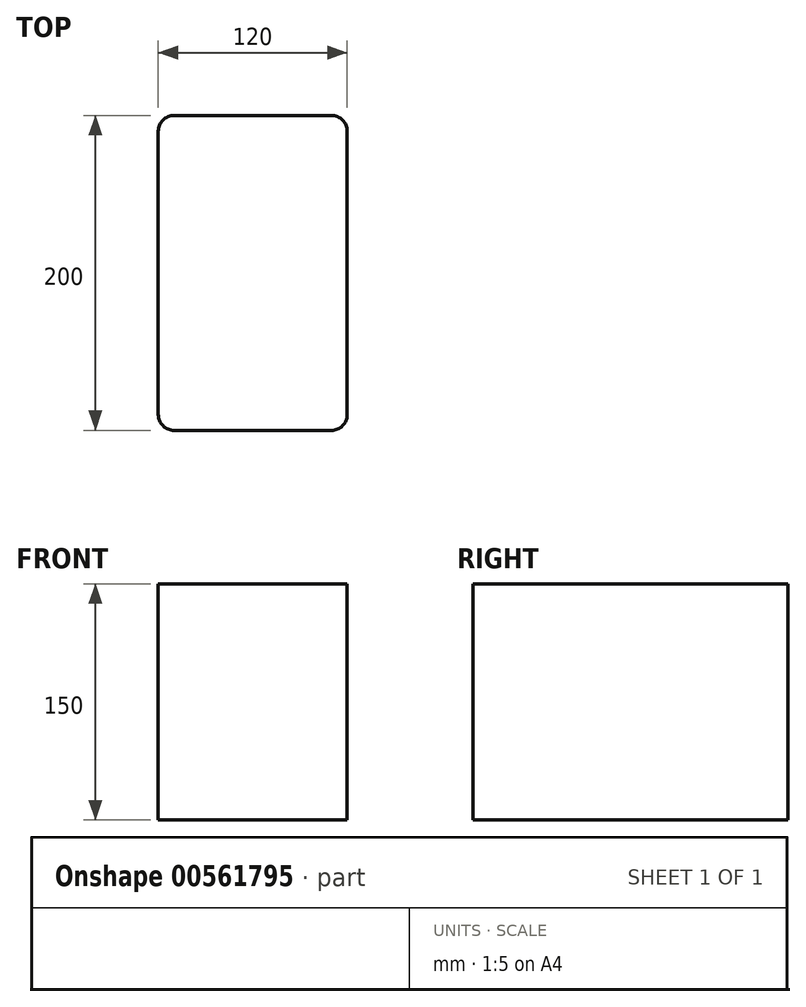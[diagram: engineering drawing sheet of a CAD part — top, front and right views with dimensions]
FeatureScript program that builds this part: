
annotation { "Feature Type Name" : "Feature", "Feature Type Description" : "" }
export const myFeature = defineFeature(function(context is Context, id is Id, definition is map)
    precondition{}
    {
        {
            var Q0;
            Q0=qCreatedBy(makeId("Top.planeOp"),FACE);
            var sketch = newSketch(context, id + "F0", { "sketchPlane" : qUnion([Q0])});
            skLineSegment(sketch, "E0.bottom", {"start": v(120, 200) * mm, "end": v(0, 200) * mm});
            skLineSegment(sketch, "E0.top", {"start": v(120, 0) * mm, "end": v(0, 0) * mm});
            skLineSegment(sketch, "E0.left", {"start": v(120, 200) * mm, "end": v(120, 0) * mm});
            skLineSegment(sketch, "E0.right", {"start": v(0, 200) * mm, "end": v(0, 0) * mm});
            skSolve(sketch);
        }
        {
            var Q0;
            Q0=makeQuery(id+"F0.imprint","IMPRINT",FACE,{"disambiguationData":[TD([[makeQuery(id+"F0.imprint","IMPRINT",EDGE,{"derivedFrom":sQuery(id+"F0.wireOp",EDGE,"E0.bottom")}),1.0]])]});
            extrude(context, id + "F1", {"entities" : qUnion([Q0]), "oppositeDirection" : true, "depth" : 150 * mm, "offsetDistance" : 25 * mm});
        }
        {
            var Q0;
            Q0=makeQuery(id+"F1.opExtrude","SWEPT_EDGE",EDGE,{"disambiguationData":[OSD([sQuery(id+"F0.wireOp",EDGE,"E0.bottom"),sQuery(id+"F0.wireOp",EDGE,"E0.left")])]});
            var Q1;
            Q1=makeQuery(id+"F1.opExtrude","SWEPT_EDGE",EDGE,{"disambiguationData":[OSD([sQuery(id+"F0.wireOp",EDGE,"E0.bottom"),sQuery(id+"F0.wireOp",EDGE,"E0.right")])]});
            var Q2;
            Q2=makeQuery(id+"F1.opExtrude","SWEPT_EDGE",EDGE,{"disambiguationData":[OSD([sQuery(id+"F0.wireOp",EDGE,"E0.top"),sQuery(id+"F0.wireOp",EDGE,"E0.right")])]});
            var Q3;
            Q3=makeQuery(id+"F1.opExtrude","SWEPT_EDGE",EDGE,{"disambiguationData":[OSD([sQuery(id+"F0.wireOp",EDGE,"E0.top"),sQuery(id+"F0.wireOp",EDGE,"E0.left")])]});
            fillet(context, id + "F2", {"entities" : qUnion([Q0, Q1, Q2, Q3]), "radius" : 10 * mm, "tangentPropagation" : true, "allowEdgeOverflow" : false});
        }
    });
